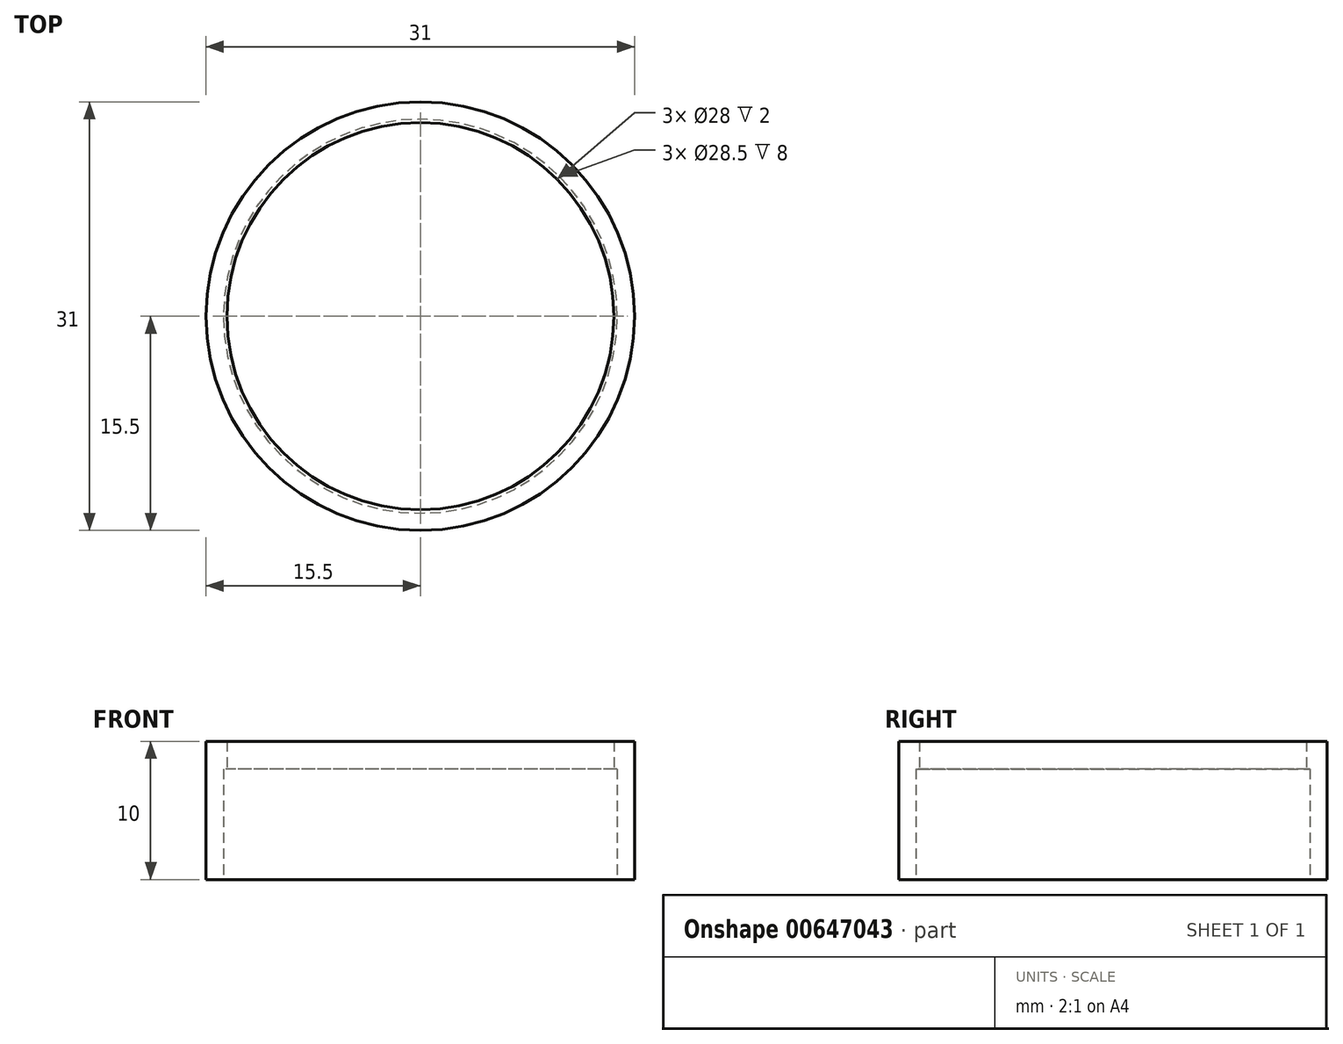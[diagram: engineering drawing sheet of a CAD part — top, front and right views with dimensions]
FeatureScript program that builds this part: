
annotation { "Feature Type Name" : "Feature", "Feature Type Description" : "" }
export const myFeature = defineFeature(function(context is Context, id is Id, definition is map)
    precondition{}
    {
        {
            var Q0;
            Q0=qCreatedBy(makeId("Top.planeOp"),FACE);
            var sketch = newSketch(context, id + "F0", { "sketchPlane" : qUnion([Q0])});
            skCircle(sketch, "E0", {"center": v(0, 0) * mm, "radius": 15.5 * mm});
            skSolve(sketch);
        }
        {
            var Q0;
            Q0 = qSketchRegion(id + "F0", true);
            extrude(context, id + "F1", {"entities" : qUnion([Q0]), "depth" : 10 * mm, "offsetDistance" : 25 * mm});
        }
        {
            var Q0;
            Q0=qCreatedBy(makeId("Top.planeOp"),FACE);
            var sketch = newSketch(context, id + "F2", { "sketchPlane" : qUnion([Q0])});
            skCircle(sketch, "E1", {"center": v(0, 0) * mm, "radius": 14 * mm});
            skSolve(sketch);
        }
        {
            var Q0;
            Q0 = qSketchRegion(id + "F2", true);
            extrude(context, id + "F3", {"entities" : qUnion([Q0]), "operationType" : NewBodyOperationType.REMOVE, "depth" : 25 * mm, "offsetDistance" : 25 * mm});
        }
        {
            var Q0;
            Q0=qCreatedBy(makeId("Top.planeOp"),FACE);
            var sketch = newSketch(context, id + "F4", { "sketchPlane" : qUnion([Q0])});
            skCircle(sketch, "E2", {"center": v(0, 0) * mm, "radius": 14.25 * mm});
            skSolve(sketch);
        }
        {
            var Q0;
            Q0 = qSketchRegion(id + "F4", true);
            extrude(context, id + "F5", {"entities" : qUnion([Q0]), "operationType" : NewBodyOperationType.REMOVE, "depth" : 8 * mm, "offsetDistance" : 25 * mm});
        }
    });
